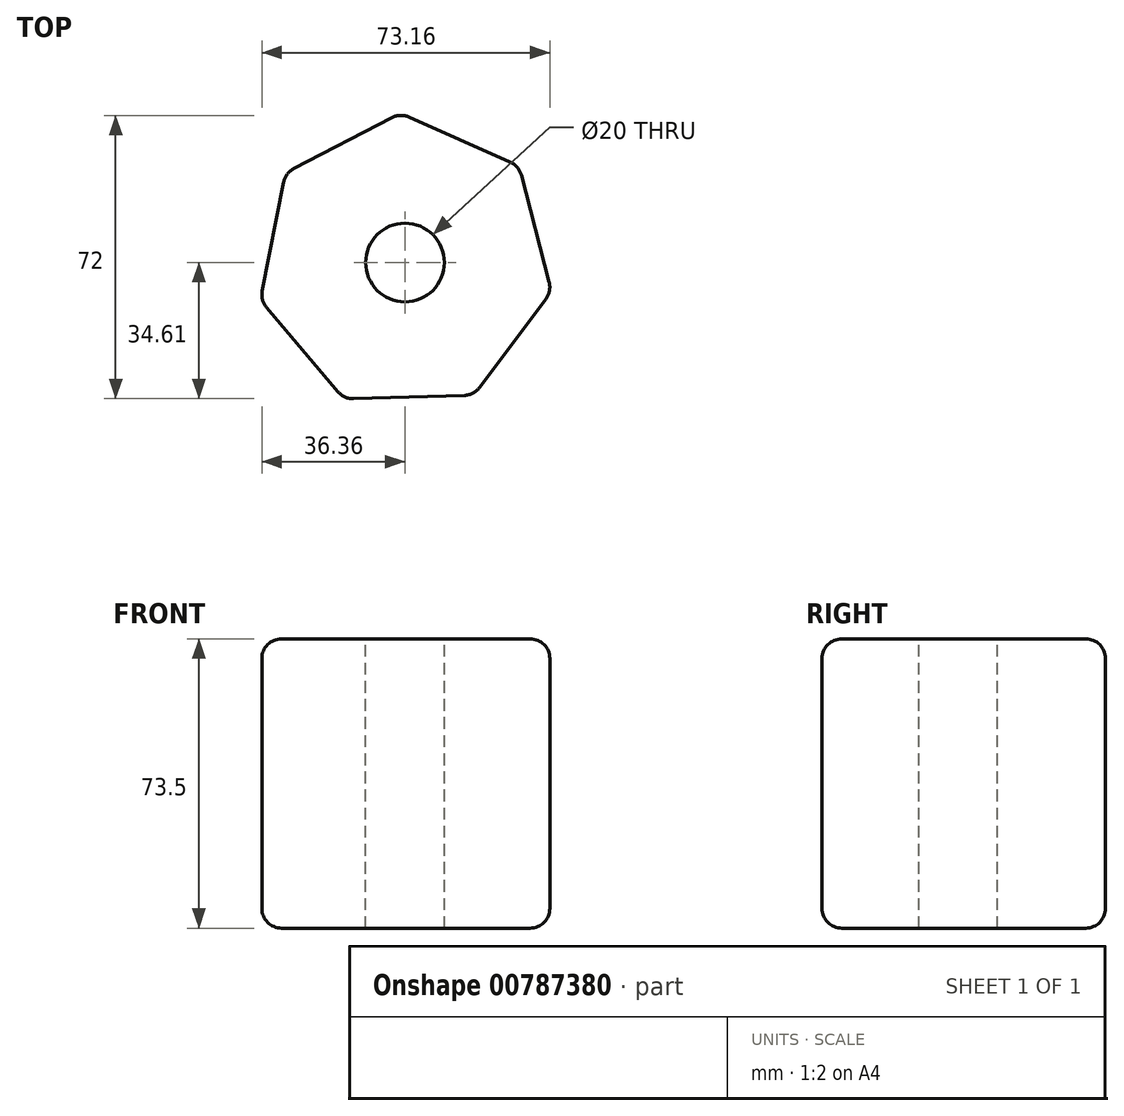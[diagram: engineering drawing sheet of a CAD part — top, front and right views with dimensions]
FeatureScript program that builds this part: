
annotation { "Feature Type Name" : "Feature", "Feature Type Description" : "" }
export const myFeature = defineFeature(function(context is Context, id is Id, definition is map)
    precondition{}
    {
        {
            var Q0;
            Q0=qCreatedBy(makeId("Top.planeOp"),FACE);
            var sketch = newSketch(context, id + "F0", { "sketchPlane" : qUnion([Q0])});
            skCircle(sketch, "E0.cCircle", {"center": v(0, 0) * mm, "radius": 34.2 * mm, "construction": true});
            skLineSegment(sketch, "E0.0", {"start": v(-30.38, 22.75) * mm, "end": v(-1.16, 37.94) * mm});
            skLineSegment(sketch, "E0.1", {"start": v(-1.16, 37.94) * mm, "end": v(28.94, 24.56) * mm});
            skLineSegment(sketch, "E0.2", {"start": v(28.94, 24.56) * mm, "end": v(37.24, -7.31) * mm});
            skLineSegment(sketch, "E0.3", {"start": v(37.24, -7.31) * mm, "end": v(17.5, -33.68) * mm});
            skLineSegment(sketch, "E0.4", {"start": v(17.5, -33.68) * mm, "end": v(-15.42, -34.68) * mm});
            skLineSegment(sketch, "E0.5", {"start": v(-15.42, -34.68) * mm, "end": v(-36.73, -9.57) * mm});
            skLineSegment(sketch, "E0.6", {"start": v(-36.73, -9.57) * mm, "end": v(-30.38, 22.75) * mm});
            skPoint(sketch, "E0.0.midPoint", {"position": v(-15.77, 30.34) * mm});
            skSolve(sketch);
        }
        {
            var Q0;
            Q0=makeQuery(id+"F0.imprint","IMPRINT",FACE,{"disambiguationData":[TD([[makeQuery(id+"F0.imprint","IMPRINT",EDGE,{"derivedFrom":sQuery(id+"F0.wireOp",EDGE,"E0.0")}),-1.0]])]});
            extrude(context, id + "F1", {"entities" : qUnion([Q0]), "depth" : 73.5 * mm, "offsetDistance" : 25 * mm});
        }
        {
            var Q0;
            Q0=makeQuery(id+"F1.opExtrude","CAP_FACE",FACE,{"disambiguationData":[OSD([sQuery(id+"F0.wireOp",EDGE,"E0.0"),sQuery(id+"F0.wireOp",EDGE,"E0.1"),sQuery(id+"F0.wireOp",EDGE,"E0.2"),sQuery(id+"F0.wireOp",EDGE,"E0.3"),sQuery(id+"F0.wireOp",EDGE,"E0.4"),sQuery(id+"F0.wireOp",EDGE,"E0.5"),sQuery(id+"F0.wireOp",EDGE,"E0.6")])],"isStart":false});
            var sketch = newSketch(context, id + "F2", { "sketchPlane" : qUnion([Q0])});
            skPoint(sketch, "E1", {"position": v(0, 0) * mm});
            skSolve(sketch);
        }
        {
            var Q0;
            Q0=sQuery(id+"F2.wireOp",VERTEX,"E1");
            var Q1;
            Q1=makeQuery(id+"F1.opExtrude","SWEPT_BODY",BODY,{"disambiguationData":[OSD([sQuery(id+"F0.wireOp",EDGE,"E0.0"),sQuery(id+"F0.wireOp",EDGE,"E0.1"),sQuery(id+"F0.wireOp",EDGE,"E0.2"),sQuery(id+"F0.wireOp",EDGE,"E0.3"),sQuery(id+"F0.wireOp",EDGE,"E0.4"),sQuery(id+"F0.wireOp",EDGE,"E0.5"),sQuery(id+"F0.wireOp",EDGE,"E0.6")])]});
            hole(context, id + "F3", {"style" : HoleStyle.C_BORE, "endStyle" : HoleEndStyle.THROUGH, "holeDiameter" : 20 * mm, "cBoreDiameter" : 20 * mm, "cBoreDepth" : 20 * mm, "majorDiameter" : 5 * mm, "isTappedThrough" : true, "tappedDepth" : 12 * mm, "tapClearance" : 3, "startFromSketch" : true, "locations" : qUnion([Q0]), "scope" : qUnion([Q1])});
        }
        {
            var Q0;
            Q0=makeQuery(id+"F1.opExtrude","CAP_EDGE",EDGE,{"disambiguationData":[OSD([sQuery(id+"F0.wireOp",EDGE,"E0.5")])],"isStart":true});
            var Q1;
            Q1=makeQuery(id+"F1.opExtrude","CAP_EDGE",EDGE,{"disambiguationData":[OSD([sQuery(id+"F0.wireOp",EDGE,"E0.6")])],"isStart":true});
            var Q2;
            Q2=makeQuery(id+"F1.opExtrude","SWEPT_EDGE",EDGE,{"disambiguationData":[OSD([sQuery(id+"F0.wireOp",EDGE,"E0.5"),sQuery(id+"F0.wireOp",EDGE,"E0.6")])]});
            var Q3;
            Q3=makeQuery(id+"F1.opExtrude","SWEPT_EDGE",EDGE,{"disambiguationData":[OSD([sQuery(id+"F0.wireOp",EDGE,"E0.4"),sQuery(id+"F0.wireOp",EDGE,"E0.5")])]});
            var Q4;
            Q4=makeQuery(id+"F1.opExtrude","CAP_EDGE",EDGE,{"disambiguationData":[OSD([sQuery(id+"F0.wireOp",EDGE,"E0.6")])],"isStart":false});
            var Q5;
            Q5=makeQuery(id+"F1.opExtrude","CAP_EDGE",EDGE,{"disambiguationData":[OSD([sQuery(id+"F0.wireOp",EDGE,"E0.5")])],"isStart":false});
            var Q6;
            Q6=makeQuery(id+"F1.opExtrude","CAP_EDGE",EDGE,{"disambiguationData":[OSD([sQuery(id+"F0.wireOp",EDGE,"E0.0")])],"isStart":false});
            var Q7;
            Q7=makeQuery(id+"F1.opExtrude","SWEPT_EDGE",EDGE,{"disambiguationData":[OSD([sQuery(id+"F0.wireOp",EDGE,"E0.0"),sQuery(id+"F0.wireOp",EDGE,"E0.6")])]});
            var Q8;
            Q8=makeQuery(id+"F1.opExtrude","SWEPT_EDGE",EDGE,{"disambiguationData":[OSD([sQuery(id+"F0.wireOp",EDGE,"E0.0"),sQuery(id+"F0.wireOp",EDGE,"E0.1")])]});
            var Q9;
            Q9=makeQuery(id+"F1.opExtrude","SWEPT_EDGE",EDGE,{"disambiguationData":[OSD([sQuery(id+"F0.wireOp",EDGE,"E0.1"),sQuery(id+"F0.wireOp",EDGE,"E0.2")])]});
            var Q10;
            Q10=makeQuery(id+"F1.opExtrude","CAP_EDGE",EDGE,{"disambiguationData":[OSD([sQuery(id+"F0.wireOp",EDGE,"E0.1")])],"isStart":false});
            var Q11;
            Q11=makeQuery(id+"F1.opExtrude","CAP_EDGE",EDGE,{"disambiguationData":[OSD([sQuery(id+"F0.wireOp",EDGE,"E0.2")])],"isStart":false});
            var Q12;
            Q12=makeQuery(id+"F1.opExtrude","CAP_EDGE",EDGE,{"disambiguationData":[OSD([sQuery(id+"F0.wireOp",EDGE,"E0.1")])],"isStart":true});
            var Q13;
            Q13=makeQuery(id+"F1.opExtrude","CAP_EDGE",EDGE,{"disambiguationData":[OSD([sQuery(id+"F0.wireOp",EDGE,"E0.2")])],"isStart":true});
            var Q14;
            Q14=makeQuery(id+"F1.opExtrude","CAP_EDGE",EDGE,{"disambiguationData":[OSD([sQuery(id+"F0.wireOp",EDGE,"E0.4")])],"isStart":true});
            var Q15;
            Q15=makeQuery(id+"F1.opExtrude","CAP_EDGE",EDGE,{"disambiguationData":[OSD([sQuery(id+"F0.wireOp",EDGE,"E0.3")])],"isStart":true});
            var Q16;
            Q16=makeQuery(id+"F1.opExtrude","SWEPT_EDGE",EDGE,{"disambiguationData":[OSD([sQuery(id+"F0.wireOp",EDGE,"E0.3"),sQuery(id+"F0.wireOp",EDGE,"E0.4")])]});
            var Q17;
            Q17=makeQuery(id+"F1.opExtrude","SWEPT_EDGE",EDGE,{"disambiguationData":[OSD([sQuery(id+"F0.wireOp",EDGE,"E0.2"),sQuery(id+"F0.wireOp",EDGE,"E0.3")])]});
            var Q18;
            Q18=makeQuery(id+"F1.opExtrude","CAP_EDGE",EDGE,{"disambiguationData":[OSD([sQuery(id+"F0.wireOp",EDGE,"E0.4")])],"isStart":false});
            var Q19;
            Q19=makeQuery(id+"F1.opExtrude","CAP_EDGE",EDGE,{"disambiguationData":[OSD([sQuery(id+"F0.wireOp",EDGE,"E0.3")])],"isStart":false});
            var Q20;
            Q20=makeQuery(id+"F3.hole-0.boolean.opBoolean","INTERSECT",EDGE,{"derivedFrom":[makeQuery(id+"F1.opExtrude","CAP_FACE",FACE,{"disambiguationData":[OSD([sQuery(id+"F0.wireOp",EDGE,"E0.0"),sQuery(id+"F0.wireOp",EDGE,"E0.1"),sQuery(id+"F0.wireOp",EDGE,"E0.2"),sQuery(id+"F0.wireOp",EDGE,"E0.3"),sQuery(id+"F0.wireOp",EDGE,"E0.4"),sQuery(id+"F0.wireOp",EDGE,"E0.5"),sQuery(id+"F0.wireOp",EDGE,"E0.6")])],"isStart":true}),makeQuery(id+"F3.hole-0.opRevolve","SWEPT_FACE",FACE,{"disambiguationData":[OSD([sQuery(id+"F3.hole-0.sketch.wireOp",EDGE,"cbore_start_line_2"),sQuery(id+"F3.hole-0.sketch.wireOp",EDGE,"core_line_2")])]})]});
            var Q21;
            Q21=makeQuery(id+"F3.hole-0.boolean.opBoolean","COPY",EDGE,{"derivedFrom":makeQuery(id+"F3.hole-0.opRevolve","SWEPT_EDGE",EDGE,{"disambiguationData":[OSD([sQuery(id+"F3.hole-0.sketch.wireOp",EDGE,"cbore_start_line_2"),sQuery(id+"F3.hole-0.sketch.wireOp",EDGE,"cbore_start_line_3")])]})});
            fillet(context, id + "F4", {"entities" : qUnion([Q0, Q1, Q2, Q3, Q4, Q5, Q6, Q7, Q8, Q9, Q10, Q11, Q12, Q13, Q14, Q15, Q16, Q17, Q18, Q19, Q20, Q21]), "radius" : 5 * mm, "tangentPropagation" : true, "allowEdgeOverflow" : false});
        }
        {
            var Q0;
            Q0=makeQuery(id+"F1.opExtrude","CAP_EDGE",EDGE,{"disambiguationData":[OSD([sQuery(id+"F0.wireOp",EDGE,"E0.0")])],"isStart":true});
            fillet(context, id + "F5", {"entities" : qUnion([Q0]), "radius" : 5 * mm, "tangentPropagation" : true, "allowEdgeOverflow" : false});
        }
    });
